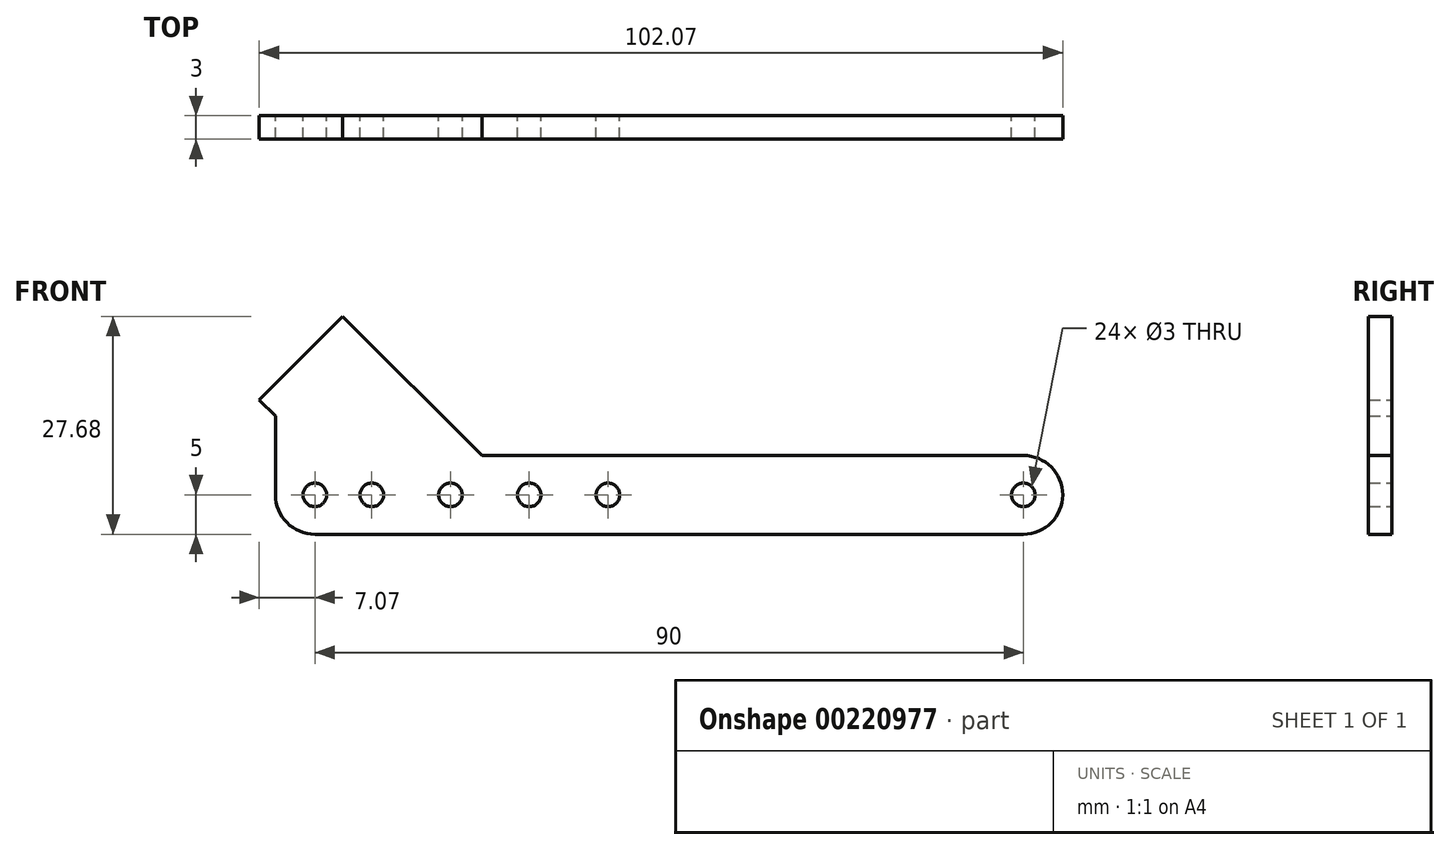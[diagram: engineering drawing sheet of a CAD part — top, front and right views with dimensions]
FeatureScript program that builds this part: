
annotation { "Feature Type Name" : "Feature", "Feature Type Description" : "" }
export const myFeature = defineFeature(function(context is Context, id is Id, definition is map)
    precondition{}
    {
        {
            var Q0;
            Q0=qCreatedBy(makeId("Front.planeOp"),FACE);
            var sketch = newSketch(context, id + "F0", { "sketchPlane" : qUnion([Q0])});
            skCircle(sketch, "E0", {"center": v(0, 0) * mm, "radius": 1.5 * mm});
            skCircle(sketch, "E1", {"center": v(90, 0) * mm, "radius": 1.5 * mm});
            skLineSegment(sketch, "E2", {"start": v(42.23, -5) * mm, "end": v(0, -5) * mm});
            skLineSegment(sketch, "E3", {"start": v(42.23, -5) * mm, "end": v(90, -5) * mm});
            skLineSegment(sketch, "E4", {"start": v(45, 5) * mm, "end": v(90, 5) * mm});
            skArc(sketch, "E5", {"start": v(90, 5) * mm, "mid": v(95, 0) * mm, "end": v(90, -5) * mm});
            skLineSegment(sketch, "E6", {"start": v(-7.07, 12.07) * mm, "end": v(3.54, 22.68) * mm});
            skLineSegment(sketch, "E7", {"start": v(3.54, 22.68) * mm, "end": v(21.21, 5) * mm});
            skLineSegment(sketch, "E8", {"start": v(21.21, 5) * mm, "end": v(45, 5) * mm});
            skLineSegment(sketch, "E9", {"start": v(-5, 0) * mm, "end": v(-5, 10) * mm});
            skLineSegment(sketch, "E10", {"start": v(-5, 10) * mm, "end": v(-7.07, 12.07) * mm});
            skArc(sketch, "E11", {"start": v(-5, 0) * mm, "mid": v(-3.54, -3.54) * mm, "end": v(0, -5) * mm});
            skCircle(sketch, "E12", {"center": v(7.23, 0) * mm, "radius": 1.5 * mm});
            skCircle(sketch, "E13", {"center": v(17.23, 0) * mm, "radius": 1.5 * mm});
            skCircle(sketch, "E14", {"center": v(27.23, 0) * mm, "radius": 1.5 * mm});
            skCircle(sketch, "E15", {"center": v(37.23, 0) * mm, "radius": 1.5 * mm});
            skSolve(sketch);
        }
        {
            var Q0;
            Q0 = qSketchRegion(id + "F0", true);
            extrude(context, id + "F1", {"entities" : qUnion([Q0]), "depth" : 3 * mm});
        }
    });
